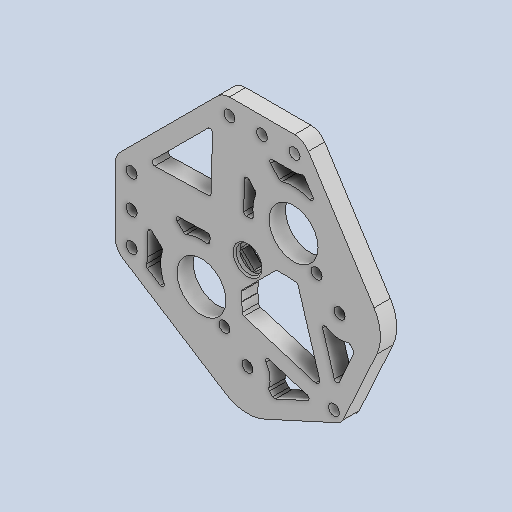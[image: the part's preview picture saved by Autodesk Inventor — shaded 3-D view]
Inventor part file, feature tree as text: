
AUTODESK INVENTOR PART (.ipt)
format: ipt  version: 2022 (Build 260153000, 153)  size: 371,200 bytes
history: native  units: in
note: dims shown in document units (in); Inventor stores cm internally (conversion verified against a paired STEP export)
features: sketch x5, other x3
ambient origin geometry x8: Origin, YZ Plane, XZ Plane, XY Plane, X Axis, Y Axis, Z Axis, Center Point
bodies: Solid1 (feature_tree)
feature tree (8):
  other  "motorplate.ipt"
  other  "Solid1::motorplate.ipt"
  other  "TaggingFeature1"
  sketch  "Sketch1"  dims[d0=0.3937in]
  sketch  "Sketch2"
  sketch  "Sketch3"
  sketch  "Sketch4"
  sketch  "Sketch5"
